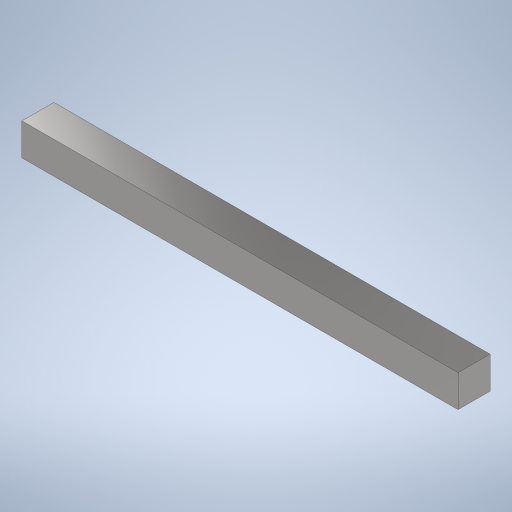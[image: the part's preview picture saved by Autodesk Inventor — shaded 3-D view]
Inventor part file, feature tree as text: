
AUTODESK INVENTOR PART (.ipt)
format: ipt  version: 2024 (Build 280153000, 153)  size: 233,472 bytes
history: native  units: in
note: dims shown in document units (in); Inventor stores cm internally (conversion verified against a paired STEP export)
features: extrude x1, sketch x1
ambient origin geometry x8: Origin, YZ Plane, XZ Plane, XY Plane, X Axis, Y Axis, Z Axis, Center Point
bodies: Solid1 (feature_tree)
feature tree (2):
  extrude  "Extrusion1"  Depth=0.25in
  sketch  "Sketch1"  dims[d0=0.25in d1=0.25in d2=3.403in d3=0.0in]
